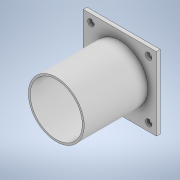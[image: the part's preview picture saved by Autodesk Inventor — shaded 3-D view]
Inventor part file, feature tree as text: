
AUTODESK INVENTOR PART (.ipt)
format: ipt  version: 2022.2 (Build 262287030, 287C)  size: 142,336 bytes
history: native  units: in
note: dims shown in document units (in); Inventor stores cm internally (conversion verified against a paired STEP export)
features: extrude x2, hole x1, sketch x1, projected_geometry x1
ambient origin geometry x8: Origin, YZ Plane, XZ Plane, XY Plane, X Axis, Y Axis, Z Axis, Center Point
bodies: Solid1 (feature_tree)
feature tree (5):
  extrude  "Extrusion1"  Depth=1.4961in
  extrude  "Extrusion2"  Depth=0.3937in
  hole  "Hole1"  [1 undecoded]
  sketch  "Sketch3"  dims[d0=1.4961in d1=1.4961in d2=0.8661in d3=0.8661in d4=0.0787in d5=0.0in d6=1.0236in d7=1.0236in d8=0.9055in d9=1.2992in d10=0.0in d11=0.5906in d12=0.5906in d13=0.7874in d15=1.1811in d16=0.7874in d18=1.1811in d21=0.1339in d22=0.2362in d23=0.1476in d24=0.0984in d25=90.0deg d26=0.3937in d27=0.8108in d28=1.063in d29=1.1417in d30=1.063in]
  projected_geometry  "Project Cut Edges1"
note: 1 required parameter value undecoded (feature->parameter linkage not recoverable at this tier; creation-order binding heuristic only, values carry confidence <= 0.55)
